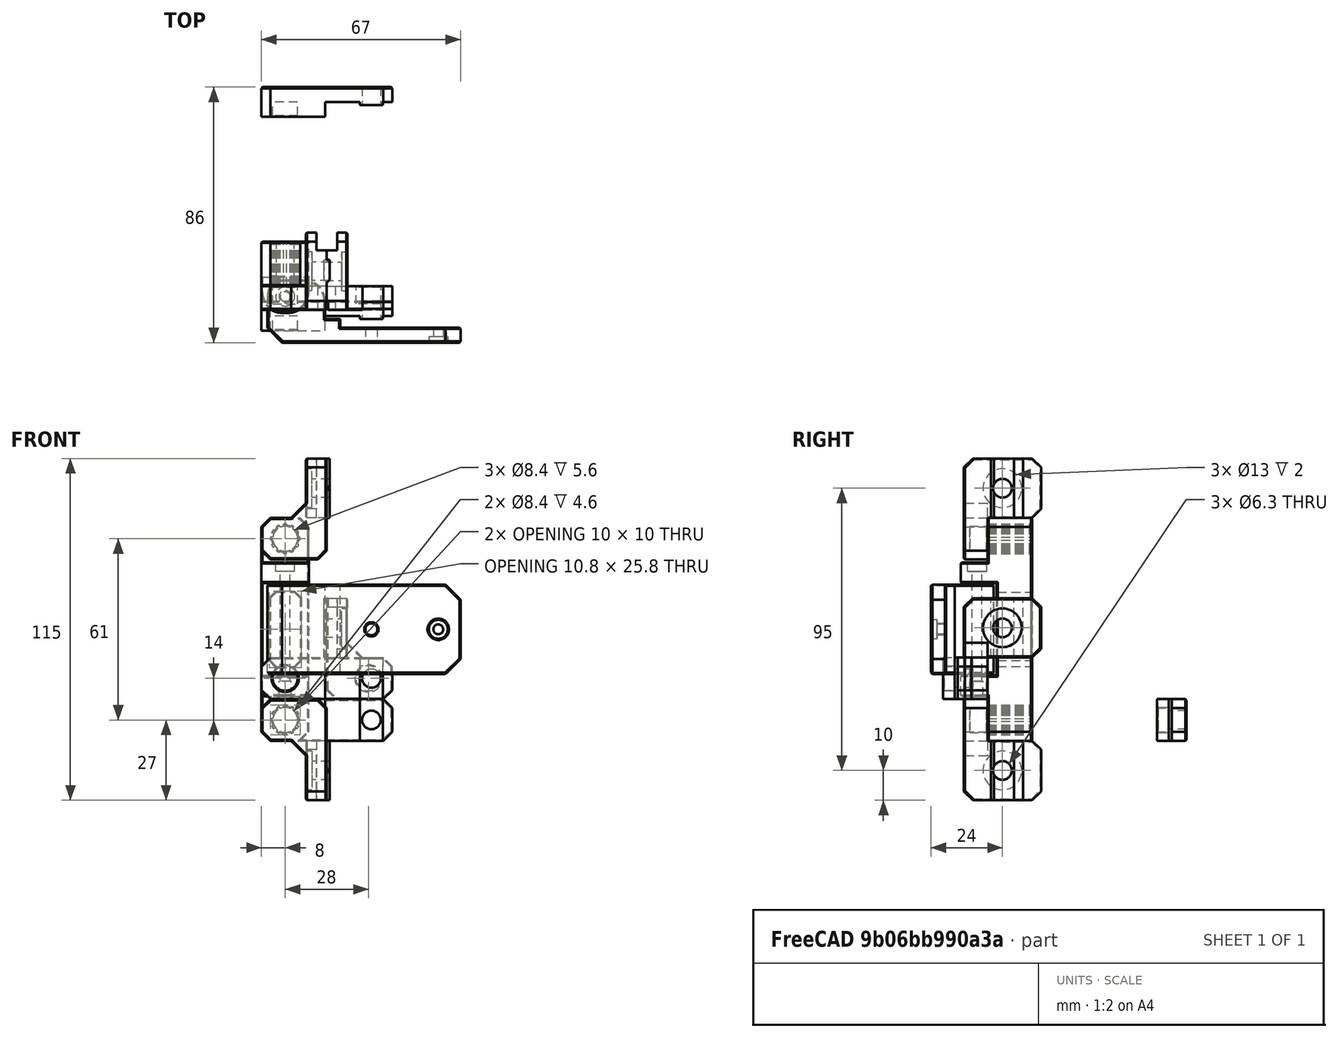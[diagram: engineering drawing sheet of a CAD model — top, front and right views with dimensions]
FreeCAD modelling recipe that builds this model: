
FCSTD DOCUMENT  (FreeCAD 0.19R24291 (Git))
Label: sliding-door-simple
License: Other
LicenseURL: GPL3
objects: Part::Box×17, Part::Chamfer×17, Part::Cut×13, Part::Cylinder×12, Part::Feature×10, Part::MultiFuse×7, Part::Refine×3, Part::Fillet×3, Part::Mirroring×2
note: 84 computed .brp shape members not serialized (recipe doc carries the construction recipe); baked Part::Feature solids carry a one-line shape summary decoded from their .brp

FEATURE [Part::Cylinder] Cylinder
  Angle = 360
  AttacherType = Attacher::AttachEngine3D
  Height = 10
  Placement = pos=(14,4,7) rot=(-1,0,0;1.5708rad)
  Radius = 4.2
FEATURE [Part::Box] Box  label="Cube"
  AttacherType = Attacher::AttachEngine3D
  Height = 14
  Length = 22
  Placement = pos=(0,2,0) rot=(0,0,1;0rad)
  Width = 8
FEATURE [Part::Box] Box001  label="Cube001"
  AttacherType = Attacher::AttachEngine3D
  Height = 20
  Length = 7
  Placement = pos=(0,2,14) rot=(0,0,1;0rad)
  Width = 26
FEATURE [Part::Cylinder] Cylinder001
  Angle = 360
  AttacherType = Attacher::AttachEngine3D
  Height = 10
  Placement = pos=(5,15,24) rot=(0,1,0;1.5708rad)
  Radius = 6.5
FEATURE [Part::Box] Box002  label="Cube002"
  AttacherType = Attacher::AttachEngine3D
  Height = 20
  Length = 3.5
  Placement = pos=(0,22,14) rot=(0,0,1;0rad)
  Width = 8
FEATURE [Part::Cut] Cut
  Base = -> Box001
  Tool = -> Box002
FEATURE [Part::Cylinder] Cylinder002
  Angle = 360
  AttacherType = Attacher::AttachEngine3D
  Height = 10
  Placement = pos=(-2,15,24) rot=(0,1,0;1.5708rad)
  Radius = 3.15
FEATURE [Part::MultiFuse] Fusion001
  Shapes = -> [Cylinder002,Cylinder001]
FEATURE [Part::Box] Box003  label="Cube003"
  AttacherType = Attacher::AttachEngine3D
  Height = 20
  Length = 2
  Placement = pos=(-1,11.1,14) rot=(0,0,1;0rad)
  Width = 7.8
FEATURE [Part::Chamfer] Chamfer003
  Base = -> Box003
  Edges = 1 edges r=1: [Edge1]
FEATURE [Part::Chamfer] Chamfer
  Base = -> Box
  Edges = 3 edges r=3: [Edge4,Edge6,Edge8]
FEATURE [Part::Chamfer] Chamfer004
  Base = -> Cut
  Edges = 3 edges r=3: [Edge7,Edge9,Edge13]
FEATURE [Part::MultiFuse] Fusion
  Shapes = -> [Chamfer,Chamfer004,Chamfer003]
FEATURE [Part::Chamfer] Chamfer005
  Base = -> Fusion
  Edges = 1 edges r=5: [Edge29]
FEATURE [Part::Cut] Cut010011008009003016026008002
  Base = -> Chamfer005
  Tool = -> Fusion001
FEATURE [Part::Cut] Cut010011008009003016026008003
  Base = -> Cut010011008009003016026008002
  Tool = -> Cylinder
FEATURE [Part::Refine] Cut010011008009003016026008003001
  Source = -> Cut010011008009003016026008003
FEATURE [Part::Chamfer] Chamfer006
  Base = -> Cut010011008009003016026008003001
  Edges = 17 edges r=0.4: [Edge15,Edge17,Edge20,Edge23,Edge28,Edge29,Edge36,Edge37,Edge39,Edge40,Edge41,Edge42,Edge43,Edge44,Edge45,Edge47,Edge73]
FEATURE [Part::Feature] Chamfer006001
  shape: bbox 23 x 26 x 34 mm, 45 faces (baked)
FEATURE [Part::Mirroring] Part__Mirroring  label="Chamfer006001 (Mirror #1)"
  Base = (0,0,0)
  Normal = (1,0,0)
  Source = -> Chamfer006001
FEATURE [Part::Mirroring] Part__Mirroring001  label="Chamfer006001 (Mirror #2)"
  Base = (0,0,0)
  Normal = (0,0,1)
  Source = -> Part__Mirroring
FEATURE [Part::Box] Box004  label="Cube004"
  AttacherType = Attacher::AttachEngine3D
  Height = 15
  Length = 16
  Placement = pos=(-22,10,-14) rot=(0,0,1;0rad)
  Width = 15
FEATURE [Part::Box] Box006  label="Cube006"
  AttacherType = Attacher::AttachEngine3D
  Height = 15
  Length = 16
  Placement = pos=(-22,10,46) rot=(0,0,1;0rad)
  Width = 15
FEATURE [Part::Box] Box007  label="Cube007"
  AttacherType = Attacher::AttachEngine3D
  Height = 47
  Length = 16
  Placement = pos=(-22,13,0) rot=(0,0,1;0rad)
  Width = 12
FEATURE [Part::Box] Box008  label="Cube008"
  AttacherType = Attacher::AttachEngine3D
  Height = 7
  Length = 16
  Placement = pos=(-22,1,1) rot=(0,0,1;0rad)
  Width = 12
FEATURE [Part::Box] Box009  label="Cube009"
  AttacherType = Attacher::AttachEngine3D
  Height = 7
  Length = 16
  Placement = pos=(-22,1,39) rot=(0,0,1;0rad)
  Width = 12
FEATURE [Part::Cylinder] Cylinder003
  Angle = 360
  AttacherType = Attacher::AttachEngine3D
  Height = 47
  Placement = pos=(-14,6.5,0) rot=(0,0,1;0rad)
  Radius = 1.65
FEATURE [Part::Cylinder] Cylinder004
  Angle = 360
  AttacherType = Attacher::AttachEngine3D
  Height = 10
  Placement = pos=(-14,6.5,43) rot=(0,0,1;0rad)
  Radius = 3.2
FEATURE [Part::MultiFuse] Fusion002
  Shapes = -> [Box004,Box008,Box007,Box009,Box006]
FEATURE [Part::Cut] Cut010011008009003016026008003002
  Base = -> Fusion002
  Tool = -> Cylinder003
FEATURE [Part::Cylinder] Cylinder005
  Angle = 360
  AttacherType = Attacher::AttachEngine3D
  Height = 10
  Placement = pos=(-14,6.5,-4) rot=(0,0,1;0rad)
  Radius = 2
FEATURE [Part::Cut] Cut010011008009003016026008003003
  Base = -> Cut010011008009003016026008003002
  Tool = -> Cylinder004
FEATURE [Part::Cut] Cut010011008009003016026008003004
  Base = -> Cut010011008009003016026008003003
  Tool = -> Cylinder005
FEATURE [Part::Chamfer] Chamfer006002
  Base = -> Cut010011008009003016026008003004
  Edges = 4 edges r=3: [Edge5,Edge16,Edge64,Edge79]
FEATURE [Part::Fillet] Fillet
  Base = -> Chamfer006002
  Edges = 4 edges r=7: [Edge20,Edge38,Edge49,Edge67]
FEATURE [Part::Box] Box010  label="Cube010"
  AttacherType = Attacher::AttachEngine3D
  Height = 25
  Length = 10
  Placement = pos=(-19,12,11) rot=(0,0,1;0rad)
  Width = 15
FEATURE [Part::Chamfer] Chamfer006003
  Base = -> Box010
  Edges = 4 edges r=2: [Edge2,Edge4,Edge6,Edge8]
FEATURE [Part::Cut] Cut010011008009003016026008003005
  Base = -> Fillet
  Tool = -> Chamfer006003
FEATURE [Part::Box] Box011  label="Cube011"
  AttacherType = Attacher::AttachEngine3D
  Height = 30
  Length = 59
  Placement = pos=(-14,-9,8.5) rot=(0,0,1;0rad)
  Width = 5
FEATURE [Part::Box] Box012  label="Cube012"
  AttacherType = Attacher::AttachEngine3D
  Height = 30
  Length = 19.5
  Placement = pos=(-20,-9,8.5) rot=(0,0,1;0rad)
  Width = 21
FEATURE [Part::Box] Box014  label="Cube013"
  AttacherType = Attacher::AttachEngine3D
  Height = 30
  Length = 5
  Placement = pos=(-0.5,-4,8.5) rot=(0,0,1;0rad)
  Width = 3
FEATURE [Part::Cylinder] Cylinder006
  Angle = 360
  AttacherType = Attacher::AttachEngine3D
  Height = 50
  Placement = pos=(-14,6.5,-4) rot=(0,0,1;0rad)
  Radius = 1.65
FEATURE [Part::MultiFuse] Fusion003
  Shapes = -> [Box011,Box014,Box012]
FEATURE [Part::Cut] Cut010011008009003016026008003006
  Base = -> Fusion003
  Tool = -> Cylinder006
FEATURE [Part::Fillet] Fillet001
  Base = -> Cut010011008009003016026008003006
  Edges = 1 edges r=5: [Edge34]
FEATURE [Part::Fillet] Fillet002
  Base = -> Fillet001
  Edges = 1 edges r=7: [Edge12]
FEATURE [Part::Chamfer] Chamfer006004
  Base = -> Fillet002
  Edges = 1 edges r=5: [Edge21]
FEATURE [Part::Chamfer] Chamfer006005
  Base = -> Chamfer006004
  Edges = 2 edges r=5: [Edge40,Edge52]
FEATURE [Part::Cylinder] Cylinder007
  Angle = 360
  AttacherType = Attacher::AttachEngine3D
  Height = 10
  Placement = pos=(15,0,23.5) rot=(1,0,0;1.5708rad)
  Radius = 2
FEATURE [Part::Cylinder] Cylinder008
  Angle = 360
  AttacherType = Attacher::AttachEngine3D
  Height = 10
  Placement = pos=(37.5,0,23.5) rot=(1,0,0;1.5708rad)
  Radius = 1.65
FEATURE [Part::Cut] Cut010011008009003016026008003007
  Base = -> Chamfer006005
  Tool = -> Cylinder007
FEATURE [Part::Cylinder] Cylinder009
  Angle = 360
  AttacherType = Attacher::AttachEngine3D
  Height = 10
  Placement = pos=(37.5,-7,23.5) rot=(1,0,0;1.5708rad)
  Radius = 3.2
FEATURE [Part::MultiFuse] Fusion004
  Shapes = -> [Cylinder009,Cylinder008]
FEATURE [Part::Cut] Cut010011008009003016026008003008
  Base = -> Cut010011008009003016026008003007
  Tool = -> Fusion004
FEATURE [Part::Refine] Cut010011008009003016026008003008001
  Source = -> Cut010011008009003016026008003008
FEATURE [Part::Chamfer] Chamfer006006
  Base = -> Cut010011008009003016026008003008001
  Edges = 31 edges r=0.4: [Edge1,Edge5,Edge6,Edge8,Edge9,Edge10,Edge13,Edge14,Edge16,Edge18,Edge19,Edge21,Edge23,Edge26,Edge27,Edge29,Edge30,Edge32,Edge33,Edge35,Edge37,Edge38,Edge39,Edge41,Edge43,Edge44,Edge45,Edge47,Edge48,Edge49,Edge51]
FEATURE [Part::Refine] Cut010011008009003016026008003005001
  Source = -> Cut010011008009003016026008003005
FEATURE [Part::Chamfer] Chamfer006007
  Base = -> Cut010011008009003016026008003005001
  Edges = 56 edges r=0.4: [Edge1,Edge2,Edge3,Edge4,Edge5,Edge9,Edge11,Edge12,Edge13,Edge14,Edge19,Edge20,Edge21,Edge22,Edge23,Edge27,Edge29,Edge31,Edge32,Edge33,Edge34,Edge35,Edge36,Edge37,Edge38,Edge39,Edge42,Edge44,Edge46,Edge47,Edge48,Edge49,Edge50,Edge53,Edge55,Edge57,Edge59,Edge62,Edge63,Edge65,Edge67,Edge69,Edge71,+13 more]
FEATURE [Part::Feature] Part__Mirroring002  label="Chamfer006001 (Mirror #1)001"
  Placement = pos=(0,0,47) rot=(0,0,1;0rad)
  shape: bbox 23 x 26 x 34 mm, 45 faces (baked)
FEATURE [Part::Box] Box015  label="Cube014"
  AttacherType = Attacher::AttachEngine3D
  Height = 14
  Length = 21.5
  Placement = pos=(-22,-5,0) rot=(0,0,1;0rad)
  Width = 5
FEATURE [Part::Box] Box016  label="Cube015"
  AttacherType = Attacher::AttachEngine3D
  Height = 14
  Length = 22
  Placement = pos=(-22,0,0) rot=(0,0,1;0rad)
  Width = 5
FEATURE [Part::Box] Box017  label="Cube016"
  AttacherType = Attacher::AttachEngine3D
  Height = 14
  Length = 22
  Width = 5
FEATURE [Part::Chamfer] Chamfer006008
  Base = -> Box016
  Edges = 2 edges r=3: [Edge2,Edge4]
FEATURE [Part::Chamfer] Chamfer006009
  Base = -> Box015
  Edges = 2 edges r=3: [Edge2,Edge4]
FEATURE [Part::Chamfer] Chamfer006012
  Base = -> Chamfer006008
  Edges = 5 edges r=0.4: [Edge3,Edge10,Edge12,Edge14,Edge15]
FEATURE [Part::Cylinder] Cylinder010
  Angle = 360
  AttacherType = Attacher::AttachEngine3D
  Height = 5
  Placement = pos=(-14,-5,7) rot=(-1,0,0;1.5708rad)
  Radius = 4.2
FEATURE [Part::Cylinder] Cylinder011
  Angle = 360
  AttacherType = Attacher::AttachEngine3D
  Height = 10
  Placement = pos=(15,8,7) rot=(1,0,0;1.5708rad)
  Radius = 3.15
FEATURE [Part::Box] Box018  label="Cube017"
  AttacherType = Attacher::AttachEngine3D
  Height = 14
  Length = 7.8
  Placement = pos=(11.1,-1,0) rot=(0,0,1;0rad)
  Width = 2
FEATURE [Part::Chamfer] Chamfer006013
  Base = -> Box017
  Edges = 2 edges r=3: [Edge6,Edge8]
FEATURE [Part::Chamfer] Chamfer006014
  Base = -> Chamfer006013
  Edges = 5 edges r=0.4: [Edge3,Edge10,Edge12,Edge14,Edge16]
FEATURE [Part::MultiFuse] Fusion005
  Shapes = -> [Chamfer006009,Chamfer006012,Chamfer006014,Box018]
FEATURE [Part::Cut] Cut010011008009003016026008003008002
  Base = -> Fusion005
  Tool = -> Cylinder011
FEATURE [Part::Cut] Cut010011008009003016026008003008003
  Base = -> Cut010011008009003016026008003008002
  Tool = -> Cylinder010
FEATURE [Part::Chamfer] Chamfer006015
  Base = -> Cut010011008009003016026008003008003
  Edges = 1 edges r=0.4: [Edge82]
FEATURE [Part::Feature] Chamfer006015001001
  Placement = pos=(0,72,-14) rot=(0,0,1;0rad)
  shape: bbox 44 x 10 x 14 mm, 28 faces (baked)
FEATURE [Part::Feature] Common001001
  Placement = pos=(-14,-2e-15,-7) rot=(-1,0,0;1.5708rad)
  shape: bbox 10 x 30 x 10 mm, 50 faces (baked)
FEATURE [Part::Feature] Common001002
  Placement = pos=(-14,-1.6e-14,54) rot=(-1,0,0;1.5708rad)
  shape: bbox 10 x 30 x 10 mm, 50 faces (baked)
FEATURE [Part::MultiFuse] Fusion006
  Shapes = -> [Common001002,Common001001]
FEATURE [Part::Cut] Cut010011008009003016026008003008004
  Base = -> Chamfer006007
  Tool = -> Fusion006
FEATURE [Part::Feature] Chamfer006015001001001
  Placement = pos=(0,72,-14) rot=(0,0,1;0rad)
  shape: bbox 44 x 10 x 14 mm, 28 faces (baked)
FEATURE [Part::Feature] Cut010011008009003016026008003008004001
  shape: bbox 16 x 24 x 75 mm, 188 faces (baked)
FEATURE [Part::Feature] Chamfer006006001
  shape: bbox 65 x 21 x 30 mm, 53 faces (baked)
FEATURE [Part::Feature] Part__Mirroring002001  label="Chamfer006001 (Mirror #1)002"
  Placement = pos=(0,0,47) rot=(0,0,1;0rad)
  shape: bbox 23 x 26 x 34 mm, 45 faces (baked)
FEATURE [Part::Feature] Part__Mirroring001001  label="Chamfer006001 (Mirror #2)001"
  shape: bbox 23 x 26 x 34 mm, 45 faces (baked)
